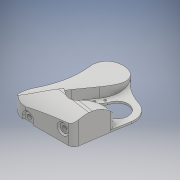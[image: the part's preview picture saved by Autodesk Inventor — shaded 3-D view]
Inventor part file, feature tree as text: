
AUTODESK INVENTOR PART (.ipt)
format: ipt  version: 2017 (Build 210142000, 142)  size: 726,528 bytes
history: native  units: mm
features: reference x28, sketch x12, extrude x10, plane x2, chamfer x2, hole x2, projected_geometry x2, boolean_combine x1
ambient origin geometry x8: Origin, YZ Plane, XZ Plane, XY Plane, X Axis, Y Axis, Z Axis, Center Point
bodies: Solid1 (feature_tree), Solid2 (feature_tree)
feature tree (59):
  extrude  "Extrusion1"  Depth=24.0mm
  extrude  "Extrusion2"  Depth=18.137236mm
  extrude  "Extrusion3"  Depth=20.0mm
  plane  "Work Plane1"
  extrude  "Extrusion4"  Depth=55.0mm
  extrude  "Extrusion5"  Depth=4.1125mm TaperAngle=0.0deg
  extrude  "Extrusion6"  Depth=22.0mm TaperAngle=0.0deg
  extrude  "Extrusion7"  Depth=88.0mm
  boolean_combine  "Combine1"
  chamfer  "Chamfer1"  Distance=128.25mm
  hole  "Hole1"  [1 undecoded]
  extrude  "Extrusion8"  Depth=34.5mm TaperAngle=0.0deg
  chamfer  "Chamfer3"  Distance=34.5mm
  plane  "Work Plane2"
  extrude  "Extrusion9"  Depth=9.0mm
  extrude  "Extrusion10"  Depth=2.0mm TaperAngle=0.0deg
  hole  "Hole2"  [1 undecoded]
  sketch  "Sketch1"  dims[d0=34.0mm d1=24.0mm]
  reference  "Reference2"
  sketch  "Sketch2"  dims[d2=17.0mm d3=18.137236mm]
  reference  "Reference3"
  reference  "Reference4"
  reference  "Reference5"
  reference  "Reference6"
  reference  "Reference7"
  projected_geometry  "Projected Loop1"
  sketch  "Sketch3"  dims[d4=6.0mm d5=20.0mm]
  projected_geometry  "Projected Loop2"
  sketch  "Sketch4"  dims[d6=115.712603mm d7=55.0mm]
  sketch  "Sketch5"  dims[d8=5.0mm d9=4.1125mm d10=0.0mm]
  sketch  "Sketch6"  dims[d11=2.1125mm d12=0.0mm d13=22.0mm d14=0.0mm]
  reference  "Reference8"
  reference  "Reference9"
  reference  "Reference10"
  reference  "Reference11"
  reference  "Reference12"
  reference  "Reference13"
  reference  "Reference14"
  reference  "Reference15"
  sketch  "Sketch7"  dims[d15=36.0mm d17=88.0mm d18=128.25mm d19=0.0mm]
  reference  "Reference16"
  reference  "Reference17"
  sketch  "Sketch8"  dims[d20=128.25mm d21=0.0mm d22=1.0mm]
  reference  "Reference18"
  reference  "Reference19"
  sketch  "Sketch9"  dims[d23=1.0mm d24=34.5mm d25=0.0mm d26=34.5mm d27=0.0mm]
  sketch  "Sketch10"  dims[d28=2.0mm d29=2.0mm d30=45.0deg]
  sketch  "Sketch12"  dims[d31=4.7mm d32=6.0mm d33=9.0mm d34=1.0mm d35=90.0deg d36=40.0mm d37=20.594885mm d41=9.0mm]
  sketch  "Sketch13"  dims[d42=9.0mm d43=1.5mm d44=0.0mm d45=1.417mm d46=2.0mm d47=45.0deg d48=-17.0mm d49=7.3mm d50=7.3mm d51=3.2mm d52=1.0mm d53=0.0mm d54=0.0mm d55=2.0mm d56=0.0mm d57=2.5mm d58=6.0mm d59=4.0mm d60=1.0mm d61=90.0deg d62=50.0mm d63=20.594885mm d64=11.4mm d65=9.561334mm]
  reference  "Reference26"
  reference  "Reference27"
  reference  "Reference28"
  reference  "Reference29"
  reference  "Reference30"
  reference  "Reference31"
  reference  "Reference32"
  reference  "Reference33"
  reference  "Reference34"
  reference  "Reference35"
note: 2 required parameter values undecoded (feature->parameter linkage not recoverable at this tier; creation-order binding heuristic only, values carry confidence <= 0.55)
